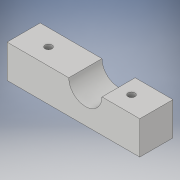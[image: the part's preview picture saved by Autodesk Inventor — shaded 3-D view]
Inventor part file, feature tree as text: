
AUTODESK INVENTOR PART (.ipt)
format: ipt  version: 2019.3 (Build 233278000, 278)  size: 113,664 bytes
history: native  units: in
note: dims shown in document units (in); Inventor stores cm internally (conversion verified against a paired STEP export)
features: sketch x4, other x3
ambient origin geometry x8: Origin, YZ Plane, XZ Plane, XY Plane, X Axis, Y Axis, Z Axis, Center Point
bodies: Solid1 (feature_tree)
feature tree (7):
  other  "HoldWormDrive.ipt"
  other  "Solid1::HoldWormDrive.ipt"
  other  "TaggingFeature1"
  sketch  "Sketch1"  dims[d0=0.3937in]
  sketch  "Sketch3"
  sketch  "Sketch4"
  sketch  "Sketch7"
